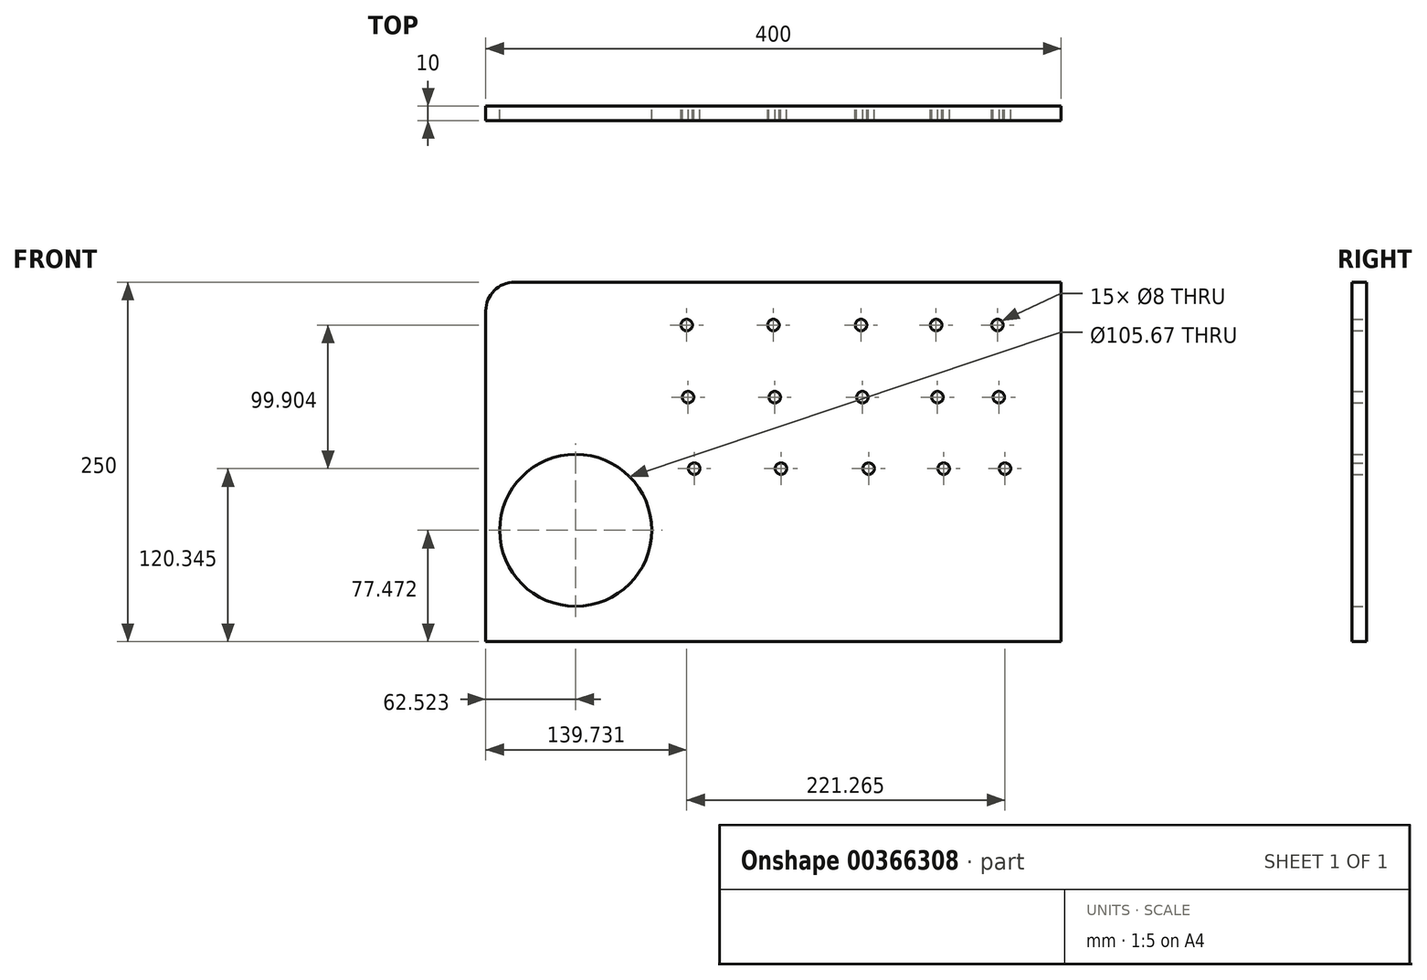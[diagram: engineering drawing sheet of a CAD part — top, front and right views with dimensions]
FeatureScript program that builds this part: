
annotation { "Feature Type Name" : "Feature", "Feature Type Description" : "" }
export const myFeature = defineFeature(function(context is Context, id is Id, definition is map)
    precondition{}
    {
        {
            var Q0;
            Q0=qCreatedBy(makeId("Front.planeOp"),FACE);
            var sketch = newSketch(context, id + "F0", { "sketchPlane" : qUnion([Q0])});
            skLineSegment(sketch, "E0.bottom", {"start": v(-180, 125) * mm, "end": v(200, 125) * mm});
            skLineSegment(sketch, "E0.top", {"start": v(-200, -125) * mm, "end": v(200, -125) * mm});
            skLineSegment(sketch, "E0.left", {"start": v(-200, 105) * mm, "end": v(-200, -125) * mm});
            skLineSegment(sketch, "E0.right", {"start": v(200, 125) * mm, "end": v(200, -125) * mm});
            skPoint(sketch, "E0.middle", {"position": v(0, 0) * mm});
            skLineSegment(sketch, "E1", {"start": v(-99.5, 95.25) * mm, "end": v(182.38, 95.25) * mm, "construction": true});
            skCircle(sketch, "E2", {"center": v(155.76, 95.25) * mm, "radius": 4 * mm});
            skPoint(sketch, "E3.visualSharp", {"position": v(-200, 125) * mm});
            skArc(sketch, "E3.filletArc", {"start": v(-180, 125) * mm, "mid": v(-194.14, 119.14) * mm, "end": v(-200, 105) * mm});
            skLineSegment(sketch, "E4", {"start": v(-98.47, 45.25) * mm, "end": v(183.41, 45.25) * mm, "construction": true});
            skLineSegment(sketch, "E5", {"start": v(-97.95, -4.75) * mm, "end": v(183.93, -4.75) * mm, "construction": true});
            skCircle(sketch, "E6", {"center": v(113.14, 95.25) * mm, "radius": 4 * mm});
            skCircle(sketch, "E7", {"center": v(60.92, 95.25) * mm, "radius": 4 * mm});
            skCircle(sketch, "E8", {"center": v(0, 95.25) * mm, "radius": 4 * mm});
            skCircle(sketch, "E9", {"center": v(-60.27, 95.25) * mm, "radius": 4 * mm});
            skCircle(sketch, "E10", {"center": v(156.7, 45.04) * mm, "radius": 4 * mm});
            skCircle(sketch, "E11", {"center": v(114.07, 45.04) * mm, "radius": 4 * mm});
            skCircle(sketch, "E12", {"center": v(61.85, 45.04) * mm, "radius": 4 * mm});
            skCircle(sketch, "E13", {"center": v(0.93, 45.04) * mm, "radius": 4 * mm});
            skCircle(sketch, "E14", {"center": v(-59.34, 45.04) * mm, "radius": 4 * mm});
            skLineSegment(sketch, "E15", {"start": v(-94.27, -4.65) * mm, "end": v(187.61, -4.65) * mm, "construction": true});
            skCircle(sketch, "E16", {"center": v(161, -4.65) * mm, "radius": 4 * mm});
            skCircle(sketch, "E17", {"center": v(118.37, -4.65) * mm, "radius": 4 * mm});
            skCircle(sketch, "E18", {"center": v(66.16, -4.65) * mm, "radius": 4 * mm});
            skCircle(sketch, "E19", {"center": v(5.24, -4.65) * mm, "radius": 4 * mm});
            skCircle(sketch, "E20", {"center": v(-55.03, -4.65) * mm, "radius": 4 * mm});
            skCircle(sketch, "E21", {"center": v(-137.48, -47.53) * mm, "radius": 52.84 * mm});
            skSolve(sketch);
        }
        {
            var Q0;
            Q0=makeQuery(id+"F0.imprint","IMPRINT",FACE,{"disambiguationData":[TD([[makeQuery(id+"F0.imprint","IMPRINT",EDGE,{"derivedFrom":sQuery(id+"F0.wireOp",EDGE,"E0.bottom")}),-1.0]])]});
            extrude(context, id + "F1", {"entities" : qUnion([Q0]), "depth" : 10 * mm});
        }
    });
